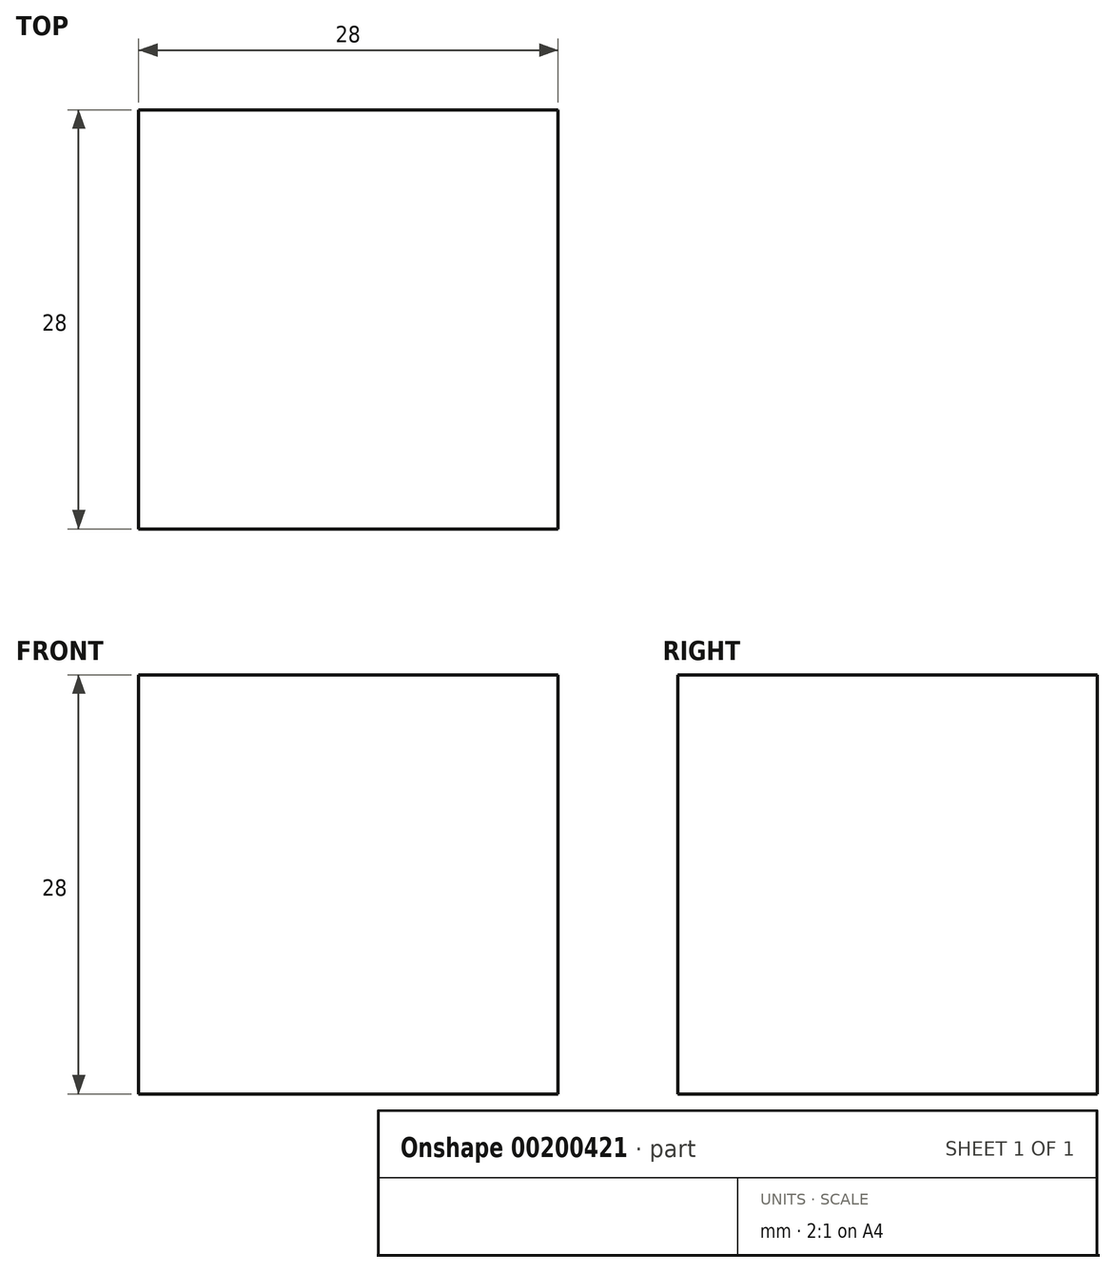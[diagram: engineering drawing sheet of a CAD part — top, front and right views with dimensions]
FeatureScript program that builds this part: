
annotation { "Feature Type Name" : "Feature", "Feature Type Description" : "" }
export const myFeature = defineFeature(function(context is Context, id is Id, definition is map)
    precondition{}
    {
        {
            var Q0;
            Q0=qCreatedBy(makeId("Top.planeOp"), FACE);
            var sketch = newSketch(context, id + "F0", { "sketchPlane" : qUnion([Q0])});
            skLineSegment(sketch, "E0.bottom", {"start": v(0, 0) * mm, "end": v(-28, 0) * mm});
            skLineSegment(sketch, "E0.top", {"start": v(0, -28) * mm, "end": v(-28, -28) * mm});
            skLineSegment(sketch, "E0.left", {"start": v(0, 0) * mm, "end": v(0, -28) * mm});
            skLineSegment(sketch, "E0.right", {"start": v(-28, 0) * mm, "end": v(-28, -28) * mm});
            skSolve(sketch);
        }
        {
            var Q0;
            Q0 = qSketchRegion(id + "F0", true);
            extrude(context, id + "F1", {"entities" : qUnion([Q0]), "depth" : 28 * mm, "offsetDistance" : 25.4 * mm});
        }
    });
